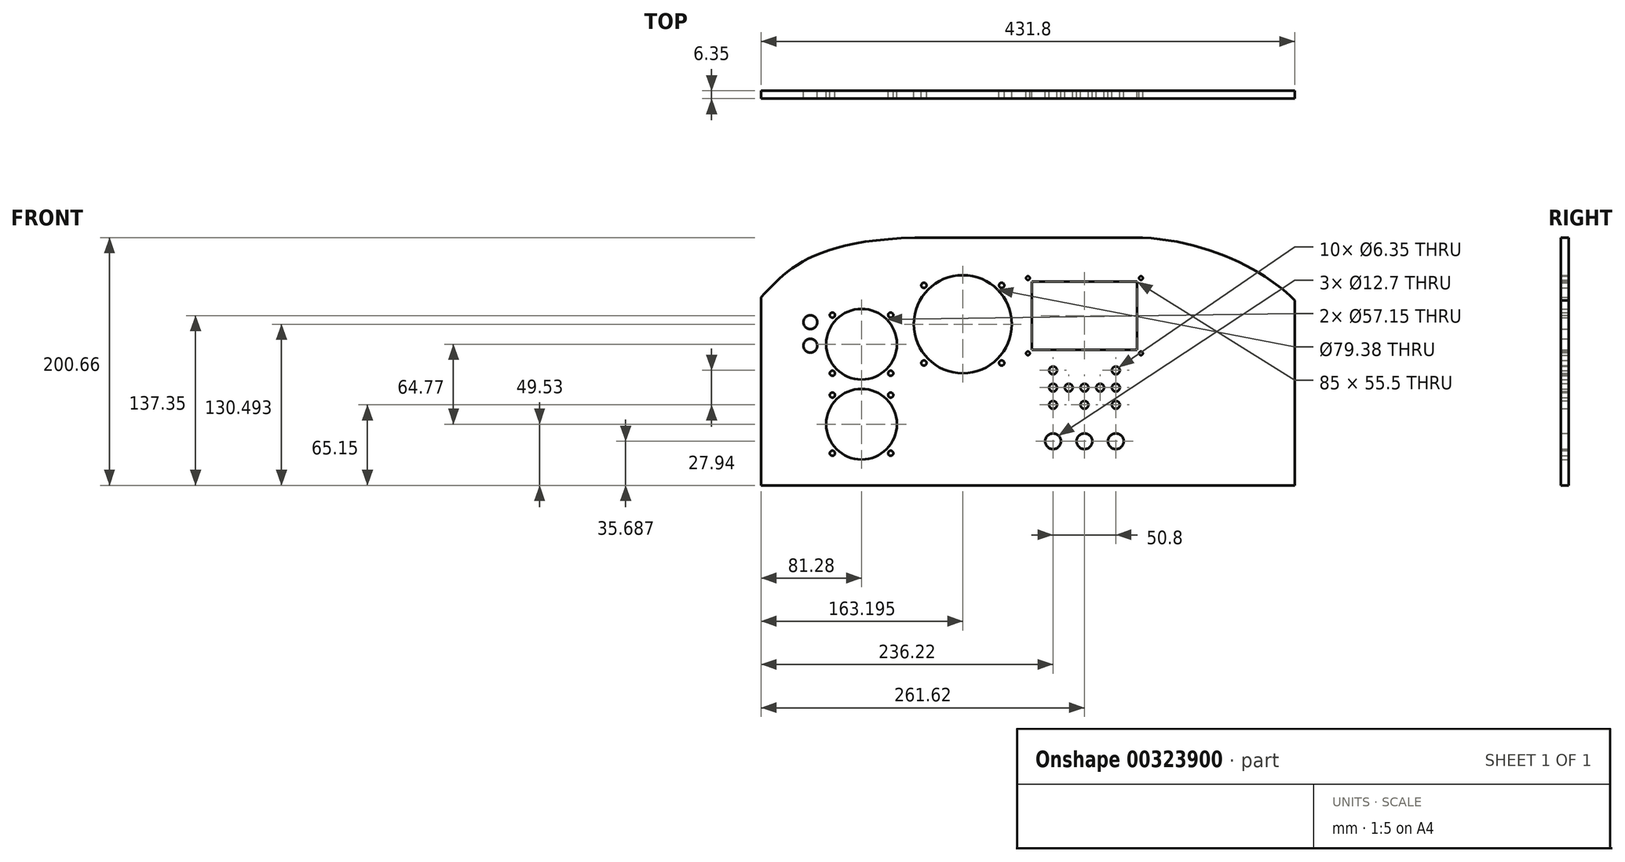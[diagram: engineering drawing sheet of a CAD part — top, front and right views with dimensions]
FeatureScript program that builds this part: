
annotation { "Feature Type Name" : "Feature", "Feature Type Description" : "" }
export const myFeature = defineFeature(function(context is Context, id is Id, definition is map)
    precondition{}
    {
        {
            var Q0;
            Q0=qCreatedBy(makeId("Front.planeOp"),FACE);
            var sketch = newSketch(context, id + "F0", { "sketchPlane" : qUnion([Q0])});
            skLineSegment(sketch, "E0.bottom", {"start": v(-215.9, 100.33) * mm, "end": v(215.9, 100.33) * mm, "construction": true});
            skLineSegment(sketch, "E0.top", {"start": v(-215.9, -100.33) * mm, "end": v(215.9, -100.33) * mm});
            skLineSegment(sketch, "E0.left", {"start": v(-215.9, 100.33) * mm, "end": v(-215.9, -100.33) * mm, "construction": true});
            skLineSegment(sketch, "E0.right", {"start": v(215.9, 100.33) * mm, "end": v(215.9, -100.33) * mm, "construction": true});
            skPoint(sketch, "E0.middle", {"position": v(0, 0) * mm});
            skLineSegment(sketch, "E1.bottom", {"start": v(-100.33, 77.79) * mm, "end": v(-5.08, 77.79) * mm, "construction": true});
            skLineSegment(sketch, "E1.top", {"start": v(-100.33, -17.46) * mm, "end": v(-5.08, -17.46) * mm, "construction": true});
            skLineSegment(sketch, "E1.left", {"start": v(-100.33, 77.79) * mm, "end": v(-100.33, -17.46) * mm, "construction": true});
            skLineSegment(sketch, "E1.right", {"start": v(-5.08, 77.79) * mm, "end": v(-5.08, -17.46) * mm, "construction": true});
            skPoint(sketch, "E1.middle", {"position": v(-52.7, 30.16) * mm});
            skLineSegment(sketch, "E2.bottom", {"start": v(-84.15, 61.61) * mm, "end": v(-21.25, 61.61) * mm, "construction": true});
            skLineSegment(sketch, "E2.top", {"start": v(-84.15, -1.29) * mm, "end": v(-21.25, -1.29) * mm, "construction": true});
            skLineSegment(sketch, "E2.left", {"start": v(-84.15, 61.61) * mm, "end": v(-84.15, -1.29) * mm, "construction": true});
            skLineSegment(sketch, "E2.right", {"start": v(-21.25, 61.61) * mm, "end": v(-21.25, -1.29) * mm, "construction": true});
            skCircle(sketch, "E3", {"center": v(-52.7, 30.16) * mm, "radius": 39.69 * mm});
            skCircle(sketch, "E4", {"center": v(-84.15, 61.61) * mm, "radius": 2.1 * mm});
            skCircle(sketch, "E5", {"center": v(-21.25, 61.61) * mm, "radius": 2.1 * mm});
            skCircle(sketch, "E6", {"center": v(-21.25, -1.29) * mm, "radius": 2.1 * mm});
            skCircle(sketch, "E7", {"center": v(-84.15, -1.29) * mm, "radius": 2.1 * mm});
            skLineSegment(sketch, "E8.bottom", {"start": v(-166.37, 45.72) * mm, "end": v(-102.87, 45.72) * mm, "construction": true});
            skLineSegment(sketch, "E8.top", {"start": v(-166.37, -17.78) * mm, "end": v(-102.87, -17.78) * mm, "construction": true});
            skLineSegment(sketch, "E8.left", {"start": v(-166.37, 45.72) * mm, "end": v(-166.37, -17.78) * mm, "construction": true});
            skLineSegment(sketch, "E8.right", {"start": v(-102.87, 45.72) * mm, "end": v(-102.87, -17.78) * mm, "construction": true});
            skPoint(sketch, "E8.middle", {"position": v(-134.62, 13.97) * mm});
            skCircle(sketch, "E9", {"center": v(-134.62, 13.97) * mm, "radius": 28.58 * mm});
            skLineSegment(sketch, "E10.bottom", {"start": v(-158.2, 37.54) * mm, "end": v(-111.05, 37.54) * mm, "construction": true});
            skLineSegment(sketch, "E10.top", {"start": v(-158.2, -9.6) * mm, "end": v(-111.05, -9.6) * mm, "construction": true});
            skLineSegment(sketch, "E10.left", {"start": v(-158.2, 37.54) * mm, "end": v(-158.2, -9.6) * mm, "construction": true});
            skLineSegment(sketch, "E10.right", {"start": v(-111.05, 37.54) * mm, "end": v(-111.05, -9.6) * mm, "construction": true});
            skCircle(sketch, "E11", {"center": v(-158.2, 37.54) * mm, "radius": 2.1 * mm});
            skCircle(sketch, "E12", {"center": v(-111.05, 37.54) * mm, "radius": 2.1 * mm});
            skCircle(sketch, "E13", {"center": v(-111.05, -9.6) * mm, "radius": 2.1 * mm});
            skCircle(sketch, "E14", {"center": v(-158.2, -9.6) * mm, "radius": 2.1 * mm});
            skLineSegment(sketch, "E15.0.1.0", {"start": v(-166.37, -19.05) * mm, "end": v(-166.37, -82.55) * mm, "construction": true});
            skPoint(sketch, "E15.0.1.1", {"position": v(-134.62, -50.8) * mm});
            skLineSegment(sketch, "E15.0.1.2", {"start": v(-166.37, -19.05) * mm, "end": v(-102.87, -19.05) * mm, "construction": true});
            skCircle(sketch, "E15.0.1.3", {"center": v(-134.62, -50.8) * mm, "radius": 28.58 * mm});
            skLineSegment(sketch, "E15.0.1.4", {"start": v(-158.2, -27.23) * mm, "end": v(-158.2, -74.37) * mm, "construction": true});
            skLineSegment(sketch, "E15.0.1.5", {"start": v(-111.05, -27.23) * mm, "end": v(-111.05, -74.37) * mm, "construction": true});
            skLineSegment(sketch, "E15.0.1.6", {"start": v(-158.2, -74.37) * mm, "end": v(-111.05, -74.37) * mm, "construction": true});
            skLineSegment(sketch, "E15.0.1.7", {"start": v(-158.2, -27.23) * mm, "end": v(-111.05, -27.23) * mm, "construction": true});
            skLineSegment(sketch, "E15.0.1.8", {"start": v(-102.87, -19.05) * mm, "end": v(-102.87, -82.55) * mm, "construction": true});
            skLineSegment(sketch, "E15.0.1.9", {"start": v(-166.37, -82.55) * mm, "end": v(-102.87, -82.55) * mm, "construction": true});
            skPoint(sketch, "E15.0.1.10", {"position": v(-134.62, -50.8) * mm});
            skCircle(sketch, "E15.0.1.11", {"center": v(-158.2, -27.23) * mm, "radius": 2.1 * mm});
            skCircle(sketch, "E15.0.1.12", {"center": v(-111.05, -74.37) * mm, "radius": 2.1 * mm});
            skCircle(sketch, "E15.0.1.13", {"center": v(-111.05, -27.23) * mm, "radius": 2.1 * mm});
            skCircle(sketch, "E15.0.1.14", {"center": v(-158.2, -74.37) * mm, "radius": 2.1 * mm});
            skLineSegment(sketch, "E15.direction1", {"start": v(-166.37, -17.78) * mm, "end": v(-149.45, -17.78) * mm, "construction": true});
            skLineSegment(sketch, "E15.direction2", {"start": v(-166.37, -17.78) * mm, "end": v(-166.37, -82.55) * mm, "construction": true});
            skPoint(sketch, "E16", {"position": v(-215.9, 52.07) * mm});
            skPoint(sketch, "E17", {"position": v(215.9, 49.53) * mm});
            skLineSegment(sketch, "E18", {"start": v(-215.9, -100.33) * mm, "end": v(-215.9, 52.07) * mm});
            skLineSegment(sketch, "E19", {"start": v(215.9, -100.33) * mm, "end": v(215.9, 49.53) * mm});
            skLineSegment(sketch, "E20", {"start": v(-79.66, 100.33) * mm, "end": v(85.44, 100.33) * mm});
            skFitSpline(sketch, "E21", {"points": [v(-79.66, 100.33) * mm, v(-215.9, 52.07) * mm], "startDerivative": vector(-284.2, 0) * mm, "endDerivative": vector(-64.7, -66.07) * mm});
            skFitSpline(sketch, "E22", {"points": [v(85.44, 100.33) * mm, v(215.9, 49.53) * mm], "startDerivative": vector(164.91, 0) * mm, "endDerivative": vector(73.9, -75.3) * mm});
            skCircle(sketch, "E23", {"center": v(-176.02, 31.75) * mm, "radius": 5.59 * mm});
            skCircle(sketch, "E24", {"center": v(-176.02, 31.75) * mm, "radius": 7.94 * mm, "construction": true});
            skCircle(sketch, "E25.0.1.0", {"center": v(-176.02, 12.7) * mm, "radius": 7.94 * mm, "construction": true});
            skCircle(sketch, "E25.0.1.1", {"center": v(-176.02, 12.7) * mm, "radius": 5.59 * mm});
            skLineSegment(sketch, "E25.direction2", {"start": v(-176.02, 31.75) * mm, "end": v(-176.02, 12.7) * mm, "construction": true});
            skLineSegment(sketch, "E26.bottom", {"start": v(3.22, 64.77) * mm, "end": v(88.22, 64.77) * mm});
            skLineSegment(sketch, "E26.top", {"start": v(3.22, 9.27) * mm, "end": v(88.22, 9.27) * mm});
            skLineSegment(sketch, "E26.left", {"start": v(3.22, 64.77) * mm, "end": v(3.22, 9.27) * mm});
            skLineSegment(sketch, "E26.right", {"start": v(88.22, 64.77) * mm, "end": v(88.22, 9.27) * mm});
            skPoint(sketch, "E26.middle", {"position": v(45.72, 37.02) * mm});
            skLineSegment(sketch, "E27.bottom", {"start": v(0, 67.5) * mm, "end": v(91.44, 67.5) * mm, "construction": true});
            skLineSegment(sketch, "E27.top", {"start": v(0, 6.54) * mm, "end": v(91.44, 6.54) * mm, "construction": true});
            skLineSegment(sketch, "E27.left", {"start": v(0, 67.5) * mm, "end": v(0, 6.54) * mm, "construction": true});
            skLineSegment(sketch, "E27.right", {"start": v(91.44, 67.5) * mm, "end": v(91.44, 6.54) * mm, "construction": true});
            skCircle(sketch, "E28", {"center": v(0, 67.5) * mm, "radius": 1.52 * mm});
            skCircle(sketch, "E29", {"center": v(91.44, 67.5) * mm, "radius": 1.52 * mm});
            skCircle(sketch, "E30", {"center": v(91.44, 6.54) * mm, "radius": 1.52 * mm});
            skCircle(sketch, "E31", {"center": v(0, 6.54) * mm, "radius": 1.52 * mm});
            skLineSegment(sketch, "E32.bottom", {"start": v(-2.54, 70.04) * mm, "end": v(93.98, 70.04) * mm, "construction": true});
            skLineSegment(sketch, "E32.top", {"start": v(-2.54, 4) * mm, "end": v(93.98, 4) * mm, "construction": true});
            skLineSegment(sketch, "E32.left", {"start": v(-2.54, 70.04) * mm, "end": v(-2.54, 4) * mm, "construction": true});
            skLineSegment(sketch, "E32.right", {"start": v(93.98, 70.04) * mm, "end": v(93.98, 4) * mm, "construction": true});
            skCircle(sketch, "E33", {"center": v(20.32, -64.64) * mm, "radius": 6.35 * mm});
            skLineSegment(sketch, "E34", {"start": v(45.72, 37.02) * mm, "end": v(45.72, -100.33) * mm, "construction": true});
            skCircle(sketch, "E35", {"center": v(20.32, -7.24) * mm, "radius": 3.18 * mm});
            skCircle(sketch, "E36.0.1.0", {"center": v(20.32, -21.2) * mm, "radius": 3.18 * mm});
            skCircle(sketch, "E36.0.2.0", {"center": v(20.32, -35.18) * mm, "radius": 3.18 * mm});
            skCircle(sketch, "E36.1.1.0", {"center": v(33.02, -21.2) * mm, "radius": 3.18 * mm});
            skCircle(sketch, "E36.2.1.0", {"center": v(45.72, -21.2) * mm, "radius": 3.18 * mm});
            skCircle(sketch, "E36.2.2.0", {"center": v(45.72, -35.18) * mm, "radius": 3.18 * mm});
            skCircle(sketch, "E36.3.1.0", {"center": v(58.42, -21.2) * mm, "radius": 3.18 * mm});
            skCircle(sketch, "E36.4.0.0", {"center": v(71.12, -7.24) * mm, "radius": 3.18 * mm});
            skCircle(sketch, "E36.4.1.0", {"center": v(71.12, -21.2) * mm, "radius": 3.18 * mm});
            skCircle(sketch, "E36.4.2.0", {"center": v(71.12, -35.18) * mm, "radius": 3.18 * mm});
            skLineSegment(sketch, "E36.direction1", {"start": v(20.32, -7.24) * mm, "end": v(33.02, -7.24) * mm, "construction": true});
            skLineSegment(sketch, "E36.direction2", {"start": v(20.32, -7.24) * mm, "end": v(20.32, -21.2) * mm, "construction": true});
            skLineSegment(sketch, "E37.bottom", {"start": v(10.8, -48) * mm, "end": v(29.85, -48) * mm, "construction": true});
            skLineSegment(sketch, "E37.top", {"start": v(10.8, -81.28) * mm, "end": v(29.85, -81.28) * mm, "construction": true});
            skLineSegment(sketch, "E37.left", {"start": v(10.8, -48) * mm, "end": v(10.8, -81.28) * mm, "construction": true});
            skLineSegment(sketch, "E37.right", {"start": v(29.85, -48) * mm, "end": v(29.85, -81.28) * mm, "construction": true});
            skLineSegment(sketch, "E38.1.0.0", {"start": v(36.2, -81.28) * mm, "end": v(55.25, -81.28) * mm, "construction": true});
            skLineSegment(sketch, "E38.1.0.1", {"start": v(55.25, -48) * mm, "end": v(55.25, -81.28) * mm, "construction": true});
            skLineSegment(sketch, "E38.1.0.2", {"start": v(36.2, -48) * mm, "end": v(55.25, -48) * mm, "construction": true});
            skCircle(sketch, "E38.1.0.3", {"center": v(45.72, -64.64) * mm, "radius": 6.35 * mm});
            skLineSegment(sketch, "E38.1.0.4", {"start": v(36.2, -48) * mm, "end": v(36.2, -81.28) * mm, "construction": true});
            skPoint(sketch, "E38.1.0.5", {"position": v(45.72, -64.64) * mm});
            skLineSegment(sketch, "E38.2.0.0", {"start": v(61.6, -81.28) * mm, "end": v(80.65, -81.28) * mm, "construction": true});
            skLineSegment(sketch, "E38.2.0.1", {"start": v(80.65, -48) * mm, "end": v(80.65, -81.28) * mm, "construction": true});
            skLineSegment(sketch, "E38.2.0.2", {"start": v(61.6, -48) * mm, "end": v(80.65, -48) * mm, "construction": true});
            skCircle(sketch, "E38.2.0.3", {"center": v(71.12, -64.64) * mm, "radius": 6.35 * mm});
            skLineSegment(sketch, "E38.2.0.4", {"start": v(61.6, -48) * mm, "end": v(61.6, -81.28) * mm, "construction": true});
            skPoint(sketch, "E38.2.0.5", {"position": v(71.12, -64.64) * mm});
            skLineSegment(sketch, "E38.direction1", {"start": v(10.8, -81.28) * mm, "end": v(36.2, -81.28) * mm, "construction": true});
            skSolve(sketch);
        }
        {
            var Q0;
            Q0 = qSketchRegion(id + "F0", true);
            extrude(context, id + "F1", {"entities" : qUnion([Q0]), "depth" : 6.35 * mm});
        }
    });
